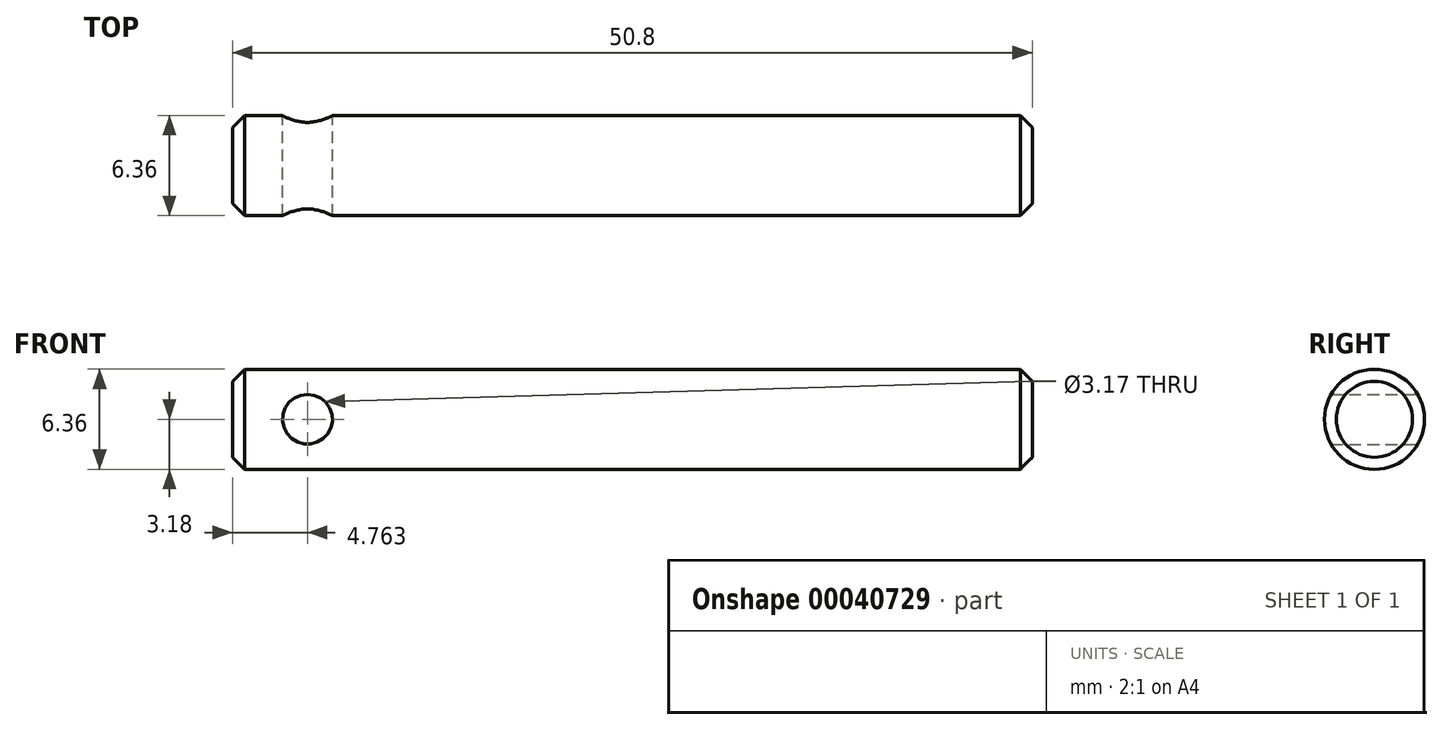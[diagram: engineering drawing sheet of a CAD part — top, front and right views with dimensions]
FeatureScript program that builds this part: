
annotation { "Feature Type Name" : "Feature", "Feature Type Description" : "" }
export const myFeature = defineFeature(function(context is Context, id is Id, definition is map)
    precondition{}
    {
        {
            var Q0;
            Q0=qCreatedBy(makeId("Right.planeOp"),FACE);
            var sketch = newSketch(context, id + "F0", { "sketchPlane" : qUnion([Q0])});
            skCircle(sketch, "E0", {"center": v(0, 0) * mm, "radius": 3.18 * mm});
            skSolve(sketch);
        }
        {
            var Q0;
            Q0=makeQuery(id+"F0.imprint","IMPRINT",FACE,{"disambiguationData":[TD([[makeQuery(id+"F0.imprint","IMPRINT",EDGE,{"derivedFrom":sQuery(id+"F0.wireOp",EDGE,"E0")}),1.0]])]});
            extrude(context, id + "F1", {"entities" : qUnion([Q0]), "depth" : 50.8 * mm});
        }
        {
            var Q0;
            Q0=makeQuery(id+"F1.opExtrude","SWEPT_FACE",FACE,{"disambiguationData":[OSD([sQuery(id+"F0.wireOp",EDGE,"E0")])]});
            chamfer(context, id + "F2", {"entities" : qUnion([Q0]), "width" : 0.76 * mm, "tangentPropagation" : true});
        }
        {
            var Q0;
            Q0=qCreatedBy(makeId("Front.planeOp"),FACE);
            var sketch = newSketch(context, id + "F3", { "sketchPlane" : qUnion([Q0])});
            skCircle(sketch, "E1", {"center": v(4.76, 0) * mm, "radius": 1.59 * mm});
            skSolve(sketch);
        }
        {
            var Q0;
            Q0 = qSketchRegion(id + "F3", true);
            extrude(context, id + "F4", {"entities" : qUnion([Q0]), "endBound" : BoundingType.SYMMETRIC, "depth" : 12.7 * mm});
        }
        {
            var Q0;
            Q0=makeQuery(id+"F4.opExtrude","SWEPT_BODY",BODY,{"disambiguationData":[OSD([sQuery(id+"F3.wireOp",EDGE,"E1")])]});
            var Q1;
            Q1=makeQuery(id+"F1.opExtrude","SWEPT_BODY",BODY,{"disambiguationData":[OSD([sQuery(id+"F0.wireOp",EDGE,"E0")])]});
            booleanBodies(context, id + "F5", {"operationType" : BooleanOperationType.SUBTRACTION, "tools" : qUnion([Q0]), "targets" : qUnion([Q1])});
        }
    });
